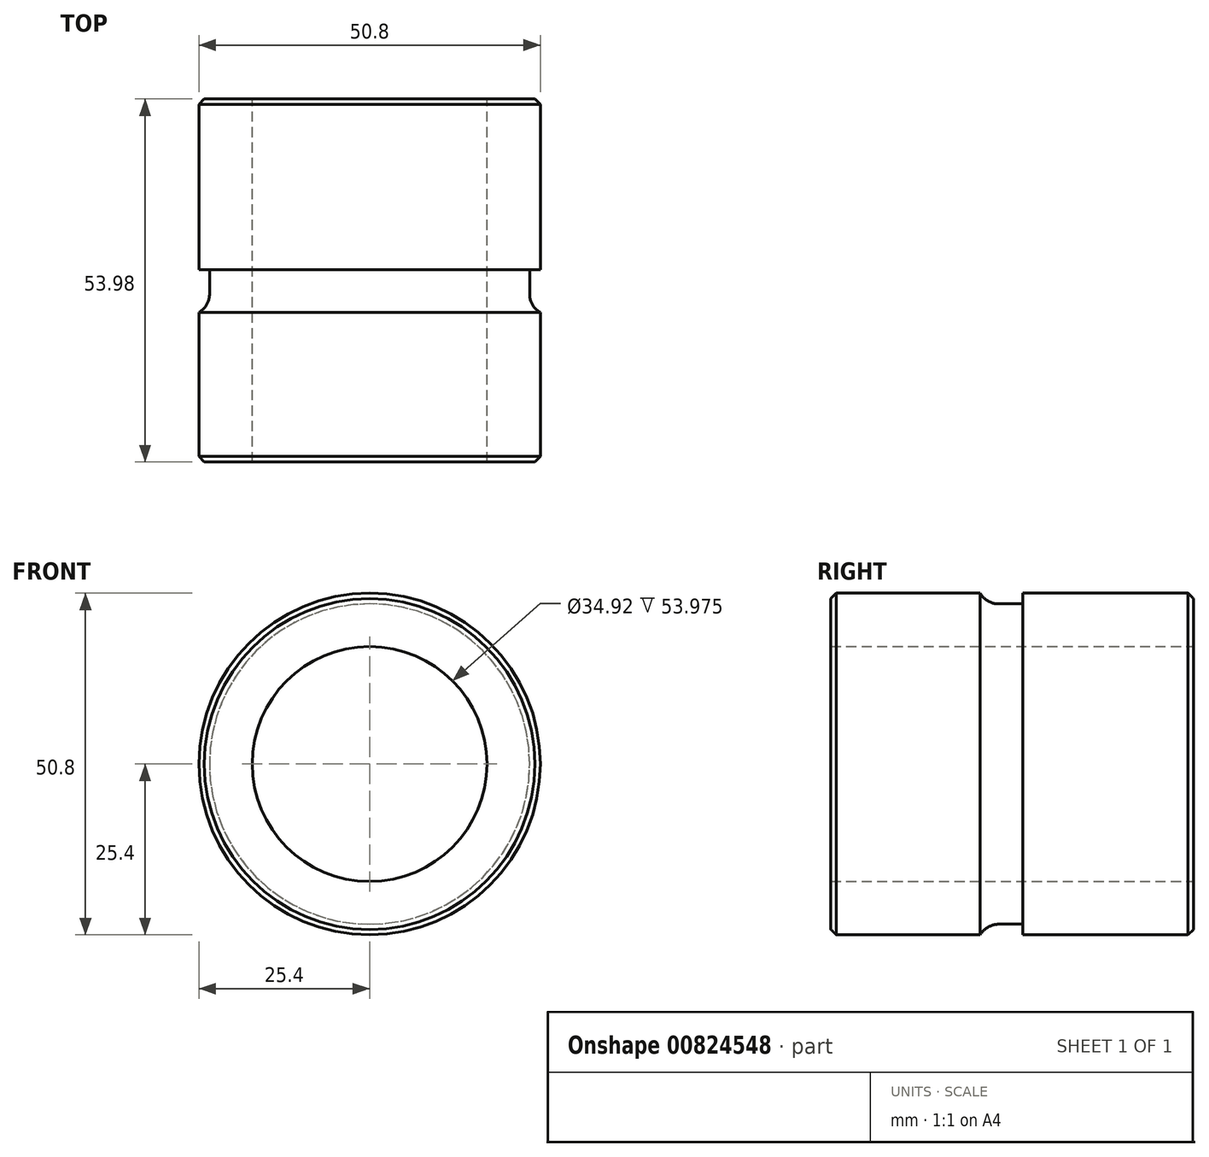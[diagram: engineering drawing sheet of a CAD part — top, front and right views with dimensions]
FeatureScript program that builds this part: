
annotation { "Feature Type Name" : "Feature", "Feature Type Description" : "" }
export const myFeature = defineFeature(function(context is Context, id is Id, definition is map)
    precondition{}
    {
        {
            var Q0;
            Q0=qCreatedBy(makeId("Front.planeOp"),FACE);
            var sketch = newSketch(context, id + "F0", { "sketchPlane" : qUnion([Q0])});
            skCircle(sketch, "E0", {"center": v(0, 0) * mm, "radius": 25.4 * mm});
            skCircle(sketch, "E1", {"center": v(0, 0) * mm, "radius": 17.46 * mm});
            skSolve(sketch);
        }
        {
            var Q0;
            Q0=makeQuery(id+"F0.imprint","IMPRINT",FACE,{"disambiguationData":[TD([[makeQuery(id+"F0.imprint","IMPRINT",EDGE,{"derivedFrom":sQuery(id+"F0.wireOp",EDGE,"E0")}),1.0]])]});
            extrude(context, id + "F1", {"entities" : qUnion([Q0]), "depth" : 25.4 * mm, "offsetDistance" : 25.4 * mm});
        }
        {
            var Q0;
            Q0=makeQuery(id+"F1.opExtrude","CAP_FACE",FACE,{"disambiguationData":[OSD([sQuery(id+"F0.wireOp",EDGE,"E0"),sQuery(id+"F0.wireOp",EDGE,"E1")])],"isStart":true});
            var sketch = newSketch(context, id + "F2", { "sketchPlane" : qUnion([Q0])});
            skCircle(sketch, "E2", {"center": v(0, 0) * mm, "radius": 23.81 * mm});
            skSolve(sketch);
        }
        {
            var Q0;
            Q0=makeQuery(id+"F2.imprint","IMPRINT",FACE,{"disambiguationData":[TD([[makeQuery(id+"F2.imprint","IMPRINT",EDGE,{"derivedFrom":sQuery(id+"F2.wireOp",EDGE,"E2")}),-1.0]])]});
            extrude(context, id + "F3", {"entities" : qUnion([Q0]), "operationType" : NewBodyOperationType.REMOVE, "oppositeDirection" : true, "depth" : 3.17 * mm, "offsetDistance" : 25.4 * mm});
        }
        {
            var Q0;
            Q0=makeQuery(id+"F1.opExtrude","CAP_FACE",FACE,{"disambiguationData":[OSD([sQuery(id+"F0.wireOp",EDGE,"E0"),sQuery(id+"F0.wireOp",EDGE,"E1")])],"isStart":true});
            extrude(context, id + "F4", {"entities" : qUnion([Q0]), "operationType" : NewBodyOperationType.ADD, "depth" : 3.17 * mm, "offsetDistance" : 25.4 * mm});
        }
        {
            var Q0;
            Q0=makeQuery(id+"F4.opExtrude","CAP_FACE",FACE,{"disambiguationData":[OSD([sQuery(id+"F0.wireOp",EDGE,"E0"),sQuery(id+"F0.wireOp",EDGE,"E1")])],"isStart":false});
            var sketch = newSketch(context, id + "F5", { "sketchPlane" : qUnion([Q0])});
            skCircle(sketch, "E3", {"center": v(0, 0) * mm, "radius": 25.4 * mm});
            skSolve(sketch);
        }
        {
            var Q0;
            Q0=qSketchRegion(id+"F5",true);
            extrude(context, id + "F6", {"entities" : qUnion([Q0]), "operationType" : NewBodyOperationType.ADD, "depth" : 25.4 * mm, "offsetDistance" : 25.4 * mm});
        }
        {
            var Q0;
            Q0=makeQuery(id+"F3.boolean.opBoolean","COPY",EDGE,{"derivedFrom":makeQuery(id+"F3.opExtrude","CAP_EDGE",EDGE,{"disambiguationData":[OSD([sQuery(id+"F2.wireOp",EDGE,"E2")])],"isStart":false})});
            var Q1;
            Q1=makeQuery(id+"F4.opExtrude","CAP_EDGE",EDGE,{"disambiguationData":[OSD([sQuery(id+"F2.wireOp",EDGE,"E2")])],"isStart":false});
            fillet(context, id + "F7", {"entities" : qUnion([Q0, Q1]), "radius" : 3.17 * mm, "tangentPropagation" : true, "allowEdgeOverflow" : false});
        }
        {
            var Q0;
            Q0=makeQuery(id+"F1.opExtrude","CAP_EDGE",EDGE,{"disambiguationData":[OSD([sQuery(id+"F0.wireOp",EDGE,"E0")])],"isStart":false});
            var Q1;
            Q1=makeQuery(id+"F6.opExtrude","CAP_FACE",FACE,{"disambiguationData":[OSD([sQuery(id+"F5.wireOp",EDGE,"E3")])],"isStart":false});
            chamfer(context, id + "F8", {"entities" : qUnion([Q0, Q1]), "width" : 0.81 * mm, "tangentPropagation" : true});
        }
        {
            var Q0;
            Q0=makeQuery(id+"F6.opExtrude","CAP_FACE",FACE,{"disambiguationData":[OSD([sQuery(id+"F5.wireOp",EDGE,"E3")])],"isStart":false});
            var sketch = newSketch(context, id + "F9", { "sketchPlane" : qUnion([Q0])});
            skCircle(sketch, "E4", {"center": v(0, 0) * mm, "radius": 17.46 * mm});
            skSolve(sketch);
        }
        {
            var Q0;
            Q0=makeQuery(id+"F9.imprint","IMPRINT",FACE,{"disambiguationData":[TD([[makeQuery(id+"F9.imprint","IMPRINT",EDGE,{"derivedFrom":sQuery(id+"F9.wireOp",EDGE,"E4")}),1.0]])]});
            extrude(context, id + "F10", {"entities" : qUnion([Q0]), "operationType" : NewBodyOperationType.REMOVE, "endBound" : BoundingType.THROUGH_ALL, "oppositeDirection" : true, "depth" : 25.4 * mm, "offsetDistance" : 25.4 * mm});
        }
    });
